# Revit family: Турникет RTD-15
name_source: partatom
category: Обобщенные модели
units: mm (PartAtom-declared; Revit-internal decimal feet)

## family parameters
Всегда вертикально = Да
Может служить основой для арматурных стержней = Нет
На основе рабочей плоскости = Нет
Общий = Нет
При загрузке вырезать с полостями = Нет
Размер круглого соединителя = Использовать диаметр
Тип детали = Нормальный
Точка расчета площади = Нет

## types (2) — shared parameters
ADSK_URL страницы изделия = https://www.perco.ru
ADSK_Единица измерения = компл.
ADSK_Завод-изготовитель = PERCo
ADSK_Количество = 1
ADSK_Масса_Текст = от 175 кг
ADSK_Материал наименование = Корпус и ротор - аллюминиевый сплав с полимерным 
порошковым покрытием
ADSK_Напряжение = от 22 В до 30 В
ADSK_Номинальная мощность = 105Вт
ADSK_Ток = 4.5А
Габаритыне размеры (длина х ширина х высота) = 1600×1800×2325 мм
Материал ротора = Сталь окрашенная RAL 1019
Материал турникета = Сталь окрашенная RAL 1019
Подключение к электросети = 220 В
Пропускная способность = 30 чел./мин
Степень защиты оболочки = IP54
Температура использования = от -40°C до +55°C
Ширина зоны прохода = 755 мм
zero-valued in all types: Отметка по умолчанию

## per-type parameters (varying)
| type | ADSK_Наименование | ADSK_Наименование краткое |
| RTD-15.1 Моторизированный | Полноростовый роторный моторизированный турникет PERCo-RTD-15 | Турникет роторный моторизированный RTD-15 |
| RTD-15.2 Электромеханический | Полноростовый роторный электромеханический турникет PERCo-RTD-15 | Турникет роторный электромеханический RTD-15 |
